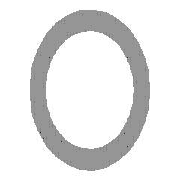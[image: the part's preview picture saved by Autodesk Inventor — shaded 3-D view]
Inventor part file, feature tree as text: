
AUTODESK INVENTOR PART (.ipt)
format: ipt  version: 2025 (Build 290162010, 162A)  size: 123,904 bytes
history: native  units: mm (DEFAULTED — no unit token found)
features: other x3, sketch x1, plane x1
ambient origin geometry x8: Origin, YZ Plane, XZ Plane, XY Plane, X Axis, Y Axis, Z Axis, Center Point
bodies: Solid1 (feature_tree), Body (feature_tree)
feature tree (5):
  other  "Driven Length"
  other  "Start plane"
  other  "End plane"
  sketch  "Sketch3"  dims[d0=88.9mm d1=2.0mm d2=300.0mm d3=0.0mm d4=-0.0mm d5=300.0mm d6=90.0deg d7=300.0mm]
  plane  "Work Plane3"
